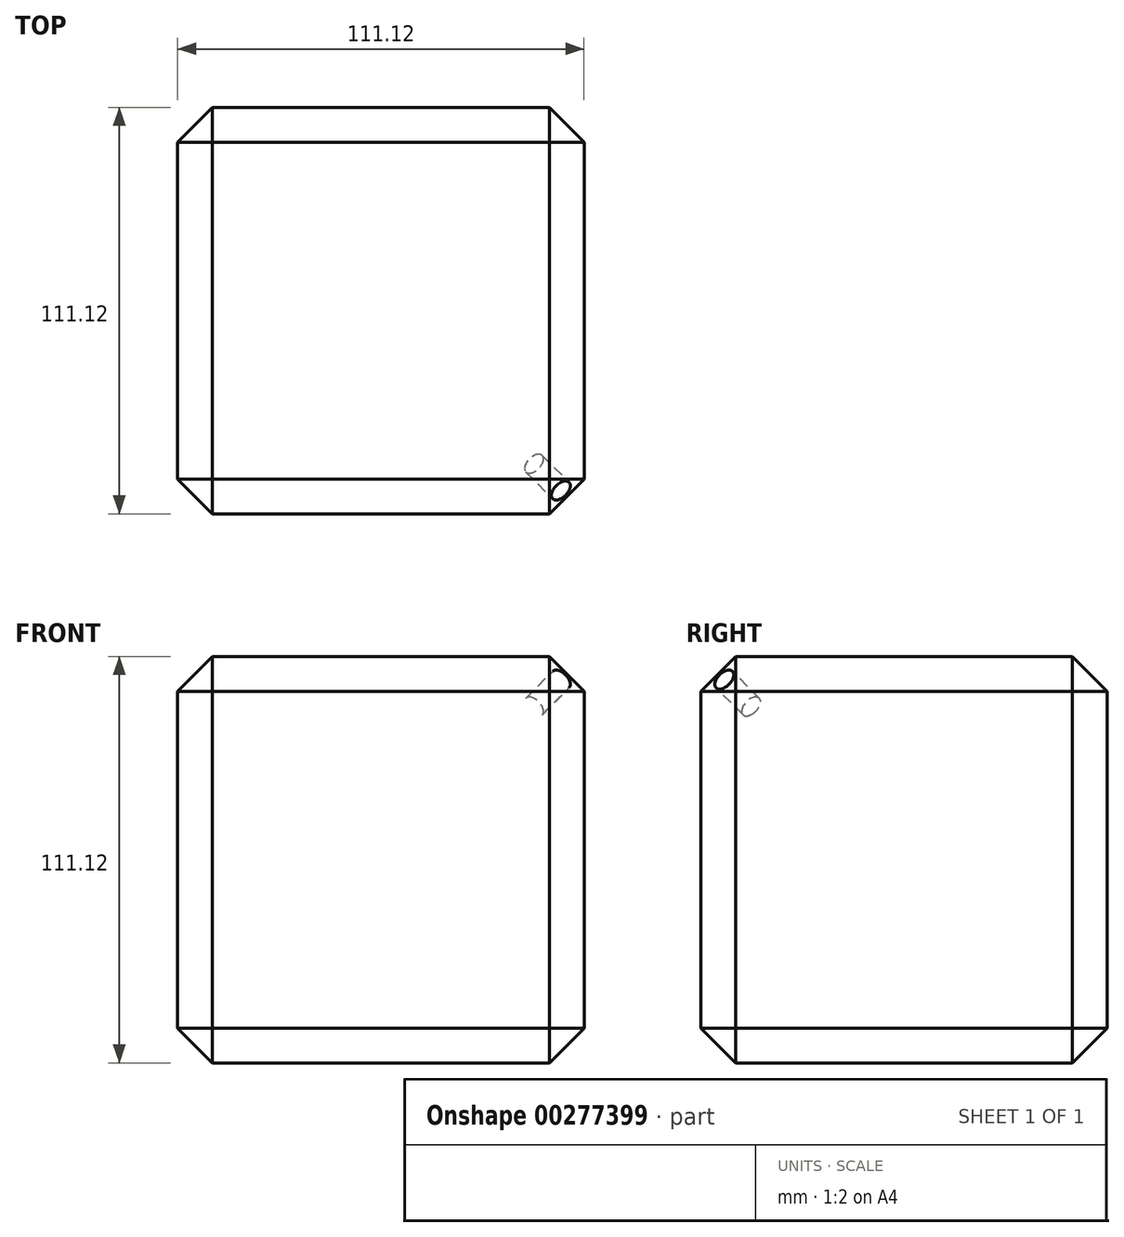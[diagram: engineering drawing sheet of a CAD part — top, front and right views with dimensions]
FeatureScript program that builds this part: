
annotation { "Feature Type Name" : "Feature", "Feature Type Description" : "" }
export const myFeature = defineFeature(function(context is Context, id is Id, definition is map)
    precondition{}
    {
        {
            var Q0;
            Q0=qCreatedBy(makeId("Top.planeOp"),FACE);
            var sketch = newSketch(context, id + "F0", { "sketchPlane" : qUnion([Q0])});
            skLineSegment(sketch, "E0.bottom", {"start": v(55.56, 55.56) * mm, "end": v(-55.56, 55.56) * mm});
            skLineSegment(sketch, "E0.top", {"start": v(55.56, -55.56) * mm, "end": v(-55.56, -55.56) * mm});
            skLineSegment(sketch, "E0.left", {"start": v(55.56, 55.56) * mm, "end": v(55.56, -55.56) * mm});
            skLineSegment(sketch, "E0.right", {"start": v(-55.56, 55.56) * mm, "end": v(-55.56, -55.56) * mm});
            skPoint(sketch, "E0.middle", {"position": v(0, 0) * mm});
            skSolve(sketch);
        }
        {
            var Q0;
            Q0 = qSketchRegion(id + "F0", true);
            extrude(context, id + "F1", {"entities" : qUnion([Q0]), "endBound" : BoundingType.SYMMETRIC, "depth" : 111.12 * mm});
        }
        {
            var Q0;
            Q0=makeQuery(id+"F1.opExtrude","CAP_EDGE",EDGE,{"disambiguationData":[OSD([sQuery(id+"F0.wireOp",EDGE,"E0.right")])],"isStart":false});
            var Q1;
            Q1=makeQuery(id+"F1.opExtrude","SWEPT_EDGE",EDGE,{"disambiguationData":[OSD([sQuery(id+"F0.wireOp",EDGE,"E0.bottom"),sQuery(id+"F0.wireOp",EDGE,"E0.right")])]});
            var Q2;
            Q2=makeQuery(id+"F1.opExtrude","SWEPT_EDGE",EDGE,{"disambiguationData":[OSD([sQuery(id+"F0.wireOp",EDGE,"E0.top"),sQuery(id+"F0.wireOp",EDGE,"E0.right")])]});
            var Q3;
            Q3=makeQuery(id+"F1.opExtrude","CAP_EDGE",EDGE,{"disambiguationData":[OSD([sQuery(id+"F0.wireOp",EDGE,"E0.right")])],"isStart":true});
            var Q4;
            Q4=makeQuery(id+"F1.opExtrude","CAP_EDGE",EDGE,{"disambiguationData":[OSD([sQuery(id+"F0.wireOp",EDGE,"E0.top")])],"isStart":true});
            var Q5;
            Q5=makeQuery(id+"F1.opExtrude","CAP_EDGE",EDGE,{"disambiguationData":[OSD([sQuery(id+"F0.wireOp",EDGE,"E0.bottom")])],"isStart":true});
            var Q6;
            Q6=makeQuery(id+"F1.opExtrude","CAP_EDGE",EDGE,{"disambiguationData":[OSD([sQuery(id+"F0.wireOp",EDGE,"E0.bottom")])],"isStart":false});
            var Q7;
            Q7=makeQuery(id+"F1.opExtrude","CAP_EDGE",EDGE,{"disambiguationData":[OSD([sQuery(id+"F0.wireOp",EDGE,"E0.top")])],"isStart":false});
            var Q8;
            Q8=makeQuery(id+"F1.opExtrude","CAP_EDGE",EDGE,{"disambiguationData":[OSD([sQuery(id+"F0.wireOp",EDGE,"E0.left")])],"isStart":false});
            var Q9;
            Q9=makeQuery(id+"F1.opExtrude","SWEPT_EDGE",EDGE,{"disambiguationData":[OSD([sQuery(id+"F0.wireOp",EDGE,"E0.top"),sQuery(id+"F0.wireOp",EDGE,"E0.left")])]});
            var Q10;
            Q10=makeQuery(id+"F1.opExtrude","CAP_EDGE",EDGE,{"disambiguationData":[OSD([sQuery(id+"F0.wireOp",EDGE,"E0.left")])],"isStart":true});
            var Q11;
            Q11=makeQuery(id+"F1.opExtrude","SWEPT_EDGE",EDGE,{"disambiguationData":[OSD([sQuery(id+"F0.wireOp",EDGE,"E0.bottom"),sQuery(id+"F0.wireOp",EDGE,"E0.left")])]});
            chamfer(context, id + "F2", {"entities" : qUnion([Q0, Q1, Q2, Q3, Q4, Q5, Q6, Q7, Q8, Q9, Q10, Q11]), "width" : 9.52 * mm, "tangentPropagation" : true});
        }
        {
            var Q0;
            {var subQ0=sQuery(id+"F0.wireOp",EDGE,"E0.left");var subQ1=sQuery(id+"F0.wireOp",EDGE,"E0.top");Q0=makeQuery(id+"F2.opChamfer","BLEND_FACE",FACE,{"disambiguationData":[OSD([subQ1,subQ0]),TDD([makeQuery(id+"F1.opExtrude","CAP_VERTEX",VERTEX,{"disambiguationData":[OSD([subQ1,subQ0])],"isStart":false})])]});}
            var sketch = newSketch(context, id + "F3", { "sketchPlane" : qUnion([Q0])});
            skCircle(sketch, "E1", {"center": v(0, 0) * mm, "radius": 3.18 * mm});
            skSolve(sketch);
        }
        {
            var Q0;
            Q0 = qSketchRegion(id + "F3", true);
            extrude(context, id + "F4", {"entities" : qUnion([Q0]), "operationType" : NewBodyOperationType.REMOVE, "oppositeDirection" : true, "depth" : 12.7 * mm});
        }
    });
